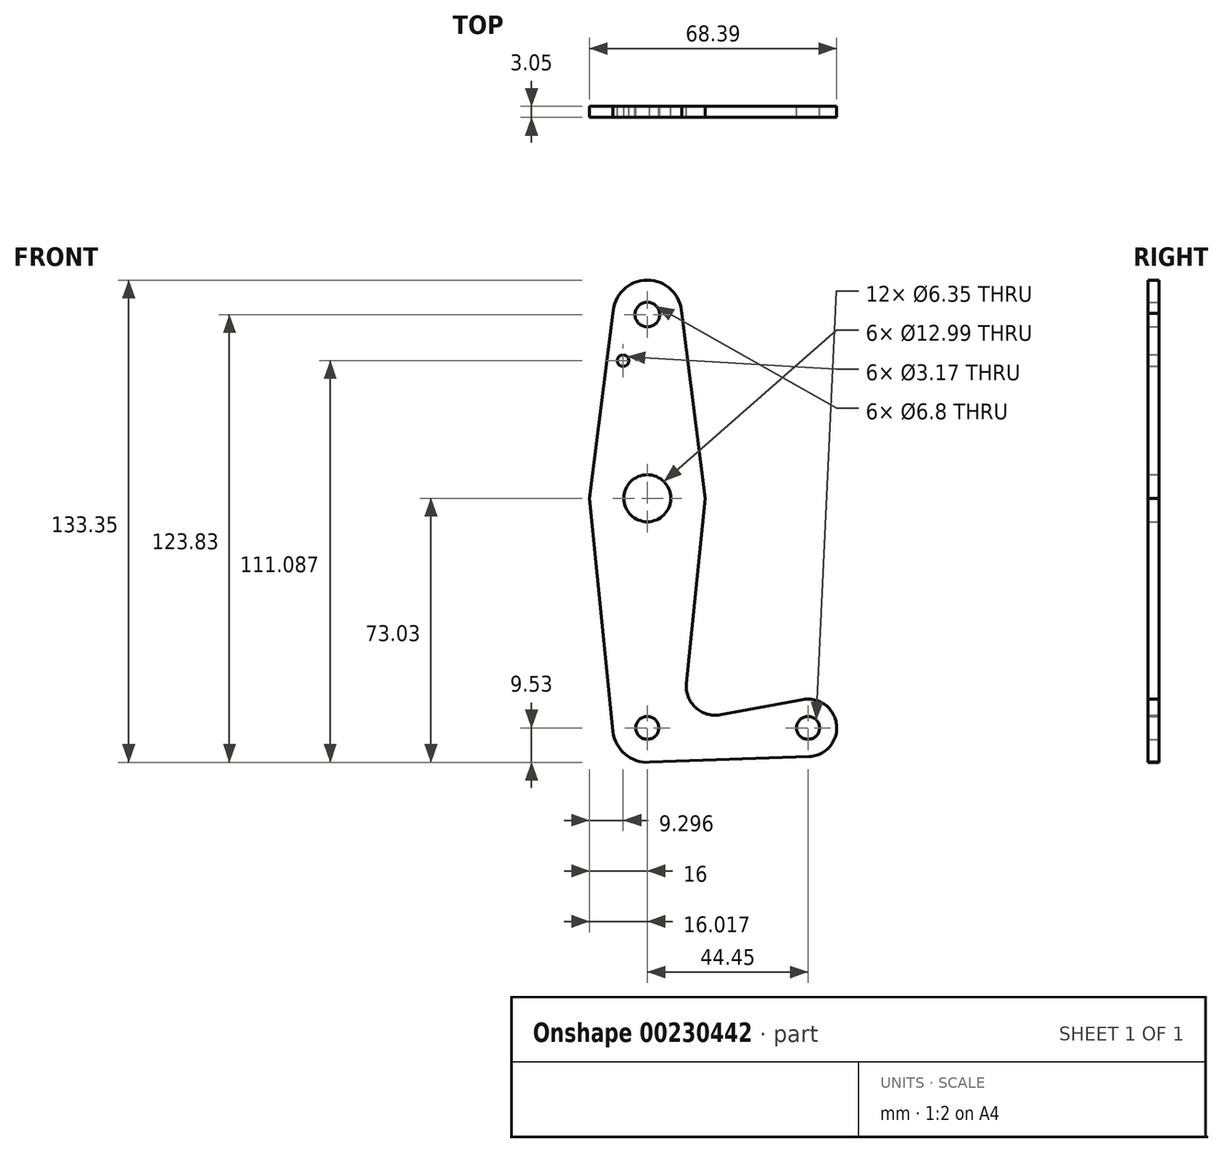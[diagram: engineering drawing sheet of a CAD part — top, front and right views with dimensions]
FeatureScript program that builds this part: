
annotation { "Feature Type Name" : "Feature", "Feature Type Description" : "" }
export const myFeature = defineFeature(function(context is Context, id is Id, definition is map)
    precondition{}
    {
        {
            var Q0;
            Q0=qCreatedBy(makeId("Front.planeOp"),FACE);
            var sketch = newSketch(context, id + "F0", { "sketchPlane" : qUnion([Q0])});
            skCircle(sketch, "E0", {"center": v(0.02, 50.8) * mm, "radius": 9.53 * mm});
            skCircle(sketch, "E1", {"center": v(0, 0) * mm, "radius": 15.88 * mm});
            skCircle(sketch, "E2", {"center": v(0, -63.5) * mm, "radius": 9.53 * mm});
            skLineSegment(sketch, "E3", {"start": v(0, -63.5) * mm, "end": v(44.45, -63.5) * mm});
            skCircle(sketch, "E4", {"center": v(44.45, -63.5) * mm, "radius": 7.94 * mm});
            skLineSegment(sketch, "E5", {"start": v(0.02, 50.8) * mm, "end": v(0, -63.5) * mm, "construction": true});
            skLineSegment(sketch, "E6", {"start": v(-9.5, 51.1) * mm, "end": v(-16, 0) * mm});
            skLineSegment(sketch, "E7", {"start": v(9.54, 51.1) * mm, "end": v(16, 0) * mm});
            skLineSegment(sketch, "E8", {"start": v(-16, 0) * mm, "end": v(-9.48, -64.46) * mm});
            skLineSegment(sketch, "E9", {"start": v(16, 0) * mm, "end": v(10.81, -51.25) * mm});
            skLineSegment(sketch, "E10", {"start": v(20.15, -59.87) * mm, "end": v(43.02, -55.7) * mm});
            skArc(sketch, "E11.filletArc", {"start": v(10.81, -51.25) * mm, "mid": v(13.33, -57.89) * mm, "end": v(20.15, -59.87) * mm});
            skLineSegment(sketch, "E12", {"start": v(0, -73.03) * mm, "end": v(44.73, -71.43) * mm});
            skCircle(sketch, "E13", {"center": v(-6.7, 38.06) * mm, "radius": 1.59 * mm});
            skCircle(sketch, "E14", {"center": v(0.02, 50.8) * mm, "radius": 3.4 * mm});
            skCircle(sketch, "E15", {"center": v(0, 0) * mm, "radius": 6.5 * mm});
            skCircle(sketch, "E16", {"center": v(0, -63.5) * mm, "radius": 3.18 * mm});
            skCircle(sketch, "E17", {"center": v(44.45, -63.5) * mm, "radius": 3.18 * mm});
            skSolve(sketch);
        }
        {
            var Q0;
            Q0 = qSketchRegion(id + "F0", true);
            extrude(context, id + "F1", {"entities" : qUnion([Q0]), "depth" : 3.05 * mm});
        }
    });
